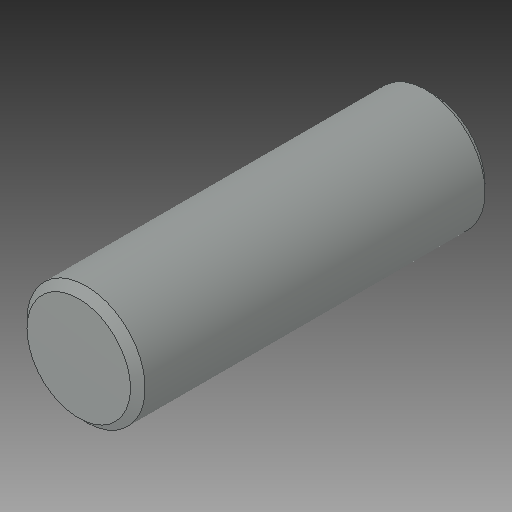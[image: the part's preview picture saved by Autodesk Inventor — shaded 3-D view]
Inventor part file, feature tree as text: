
AUTODESK INVENTOR PART (.ipt)
format: ipt  version: 2017 (Build 210142000, 142)  size: 98,304 bytes
history: native  units: in
note: dims shown in document units (in); Inventor stores cm internally (conversion verified against a paired STEP export)
features: chamfer x1
ambient origin geometry x8: Origin, YZ Plane, XZ Plane, XY Plane, X Axis, Y Axis, Z Axis, Center Point
bodies: Solid1 (feature_tree)
feature tree (1):
  chamfer  "Chamfer1"  [1 undecoded]
note: 1 required parameter value undecoded (feature->parameter linkage not recoverable at this tier; creation-order binding heuristic only, values carry confidence <= 0.55)
